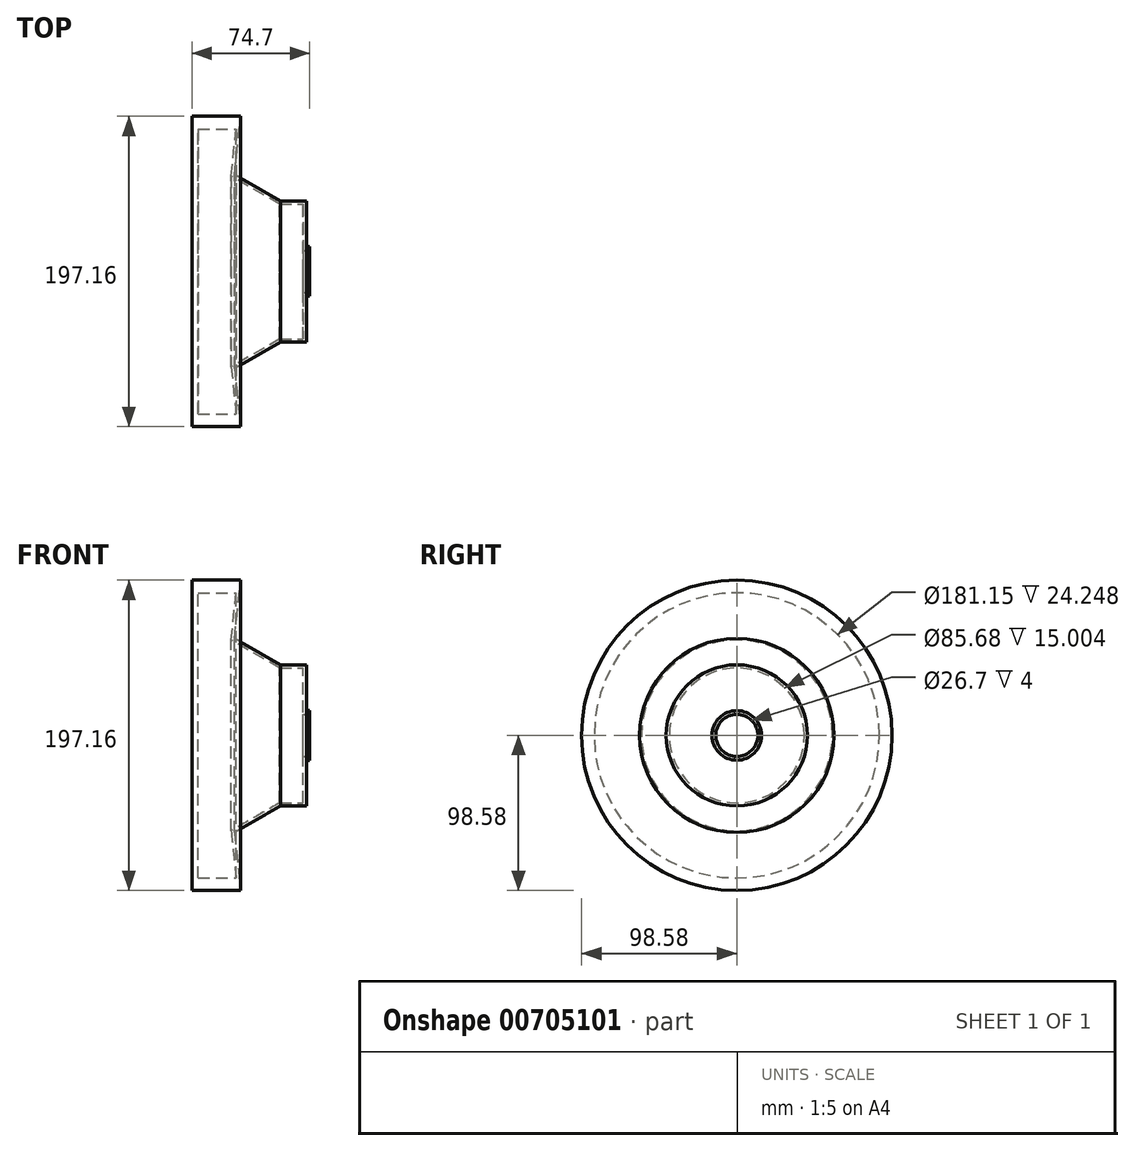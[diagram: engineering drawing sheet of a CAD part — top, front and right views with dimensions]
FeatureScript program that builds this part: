
annotation { "Feature Type Name" : "Feature", "Feature Type Description" : "" }
export const myFeature = defineFeature(function(context is Context, id is Id, definition is map)
    precondition{}
    {
        {
            var Q0;
            Q0=qCreatedBy(makeId("Front.planeOp"),FACE);
            var sketch = newSketch(context, id + "F0", { "sketchPlane" : qUnion([Q0])});
            skLineSegment(sketch, "E0", {"start": v(0, 0) * mm, "end": v(0, 98.58) * mm});
            skLineSegment(sketch, "E1", {"start": v(0, 98.58) * mm, "end": v(30.9, 98.58) * mm});
            skLineSegment(sketch, "E2", {"start": v(30.9, 98.58) * mm, "end": v(27.02, 61.7) * mm});
            skLineSegment(sketch, "E3", {"start": v(27.02, 61.7) * mm, "end": v(56.23, 44.84) * mm});
            skLineSegment(sketch, "E4", {"start": v(56.23, 44.84) * mm, "end": v(72.7, 44.84) * mm});
            skLineSegment(sketch, "E5", {"start": v(72.7, 44.84) * mm, "end": v(72.7, 15.75) * mm});
            skLineSegment(sketch, "E6", {"start": v(72.7, 15.75) * mm, "end": v(74.7, 15.75) * mm});
            skLineSegment(sketch, "E7", {"start": v(74.7, 15.75) * mm, "end": v(74.7, 13.35) * mm});
            skLineSegment(sketch, "E8", {"start": v(74.7, 13.35) * mm, "end": v(70.7, 13.35) * mm});
            skLineSegment(sketch, "E9", {"start": v(70.7, 13.35) * mm, "end": v(70.7, 42.84) * mm});
            skLineSegment(sketch, "E10", {"start": v(70.7, 42.84) * mm, "end": v(55.7, 42.84) * mm});
            skLineSegment(sketch, "E11", {"start": v(55.7, 42.84) * mm, "end": v(24.9, 60.62) * mm});
            skLineSegment(sketch, "E12", {"start": v(24.9, 60.62) * mm, "end": v(28.05, 90.58) * mm});
            skLineSegment(sketch, "E13", {"start": v(28.05, 90.58) * mm, "end": v(3.8, 90.58) * mm});
            skLineSegment(sketch, "E14", {"start": v(3.8, 90.58) * mm, "end": v(3.8, 0) * mm});
            skLineSegment(sketch, "E15", {"start": v(3.8, 0) * mm, "end": v(0, 0) * mm});
            skSolve(sketch);
        }
        {
            var Q0;
            Q0=makeQuery(id+"F0.imprint","IMPRINT",FACE,{"disambiguationData":[TD([[makeQuery(id+"F0.imprint","IMPRINT",EDGE,{"derivedFrom":sQuery(id+"F0.wireOp",EDGE,"E0")}),-1.0]])]});
            var Q1;
            Q1=sQuery(id+"F0.wireOp",EDGE,"E15");
            revolve(context, id + "F1", {"surfaceOperationType" : NewSurfaceOperationType.NEW, "entities" : qUnion([Q0]), "axis" : qUnion([Q1]), "revolveType" : RevolveType.FULL});
        }
    });
